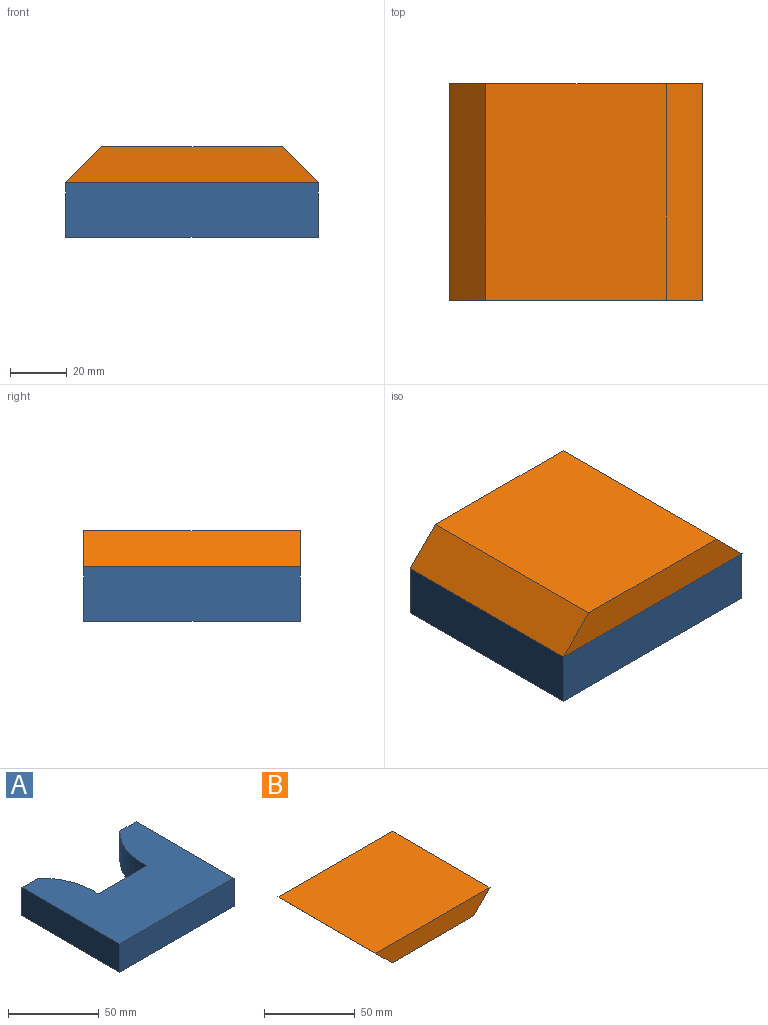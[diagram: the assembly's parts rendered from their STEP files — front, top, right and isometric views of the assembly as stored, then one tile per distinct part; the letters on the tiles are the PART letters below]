
ASSEMBLY  parts=2 mates=1
PART A: 10 faces, bbox 88.9x76.2x19.1 mm
  f0: plane 19.05x12.7mm, normal (0,1,0), area 241.9mm2, adj f1,f7,f8,f9
  f1: cylinder r=41.23mm len=33.83mm, axis (0,0,-1), area 712.5mm2, adj f0,f2,f8,f9
  f2: plane 38.1x19.05mm, normal (0,1,0), area 725.8mm2, adj f1,f3,f8,f9
  f3: cylinder r=41.23mm len=33.83mm, axis (0,0,-1), area 712.5mm2, adj f2,f4,f8,f9
  f4: plane 19.05x12.7mm, normal (0,1,0), area 241.9mm2, adj f3,f5,f8,f9
  f5: plane 76.2x19.05mm, normal (-1,0,0), area 1451.6mm2, adj f4,f6,f8,f9
  f6: plane 88.9x19.05mm, normal (0,-1,0), area 1693.5mm2, adj f5,f7,f8,f9
  f7: plane 76.2x19.05mm, normal (1,0,0), area 1451.6mm2, adj f0,f6,f8,f9
  f8: plane 88.9x76.2mm, normal (0,0,1), area 5258.7mm2, adj f0,f1,f2,f3,f4,f5,f6,f7
  f9: plane 88.9x76.2mm, normal (0,0,-1), area 5258.7mm2, adj f0,f1,f2,f3,f4,f5,f6,f7
PART B: 6 faces, bbox 88.9x76.2x12.7 mm
  f0: plane 88.9x76.2mm, normal (0,0,1), area 6774.2mm2, adj f1,f3,f4,f5
  f1: plane 76.2x12.7mm, normal (-0.71,0,-0.71), area 1368.6mm2, adj f0,f2,f4,f5
  f2: plane 76.2x63.5mm, normal (0,0,-1), area 4838.7mm2, adj f1,f3,f4,f5
  f3: plane 76.2x12.7mm, normal (0.71,0,-0.71), area 1368.6mm2, adj f0,f2,f4,f5
  f4: plane 88.9x12.7mm, normal (0,-1,0), area 967.7mm2, adj f0,f1,f2,f3
  f5: plane 88.9x12.7mm, normal (0,1,0), area 967.7mm2, adj f0,f1,f2,f3
PLACE A t=(-102,5.54,-67.9)mm
PLACE B rot(axis=(1,0,0),180deg) t=(-102,-70.66,-33.82)mm
MATE fastened B.f0 <-> A.f8  axis (0,0,-1) through (-96.75,-32.56,-48.85)mm
